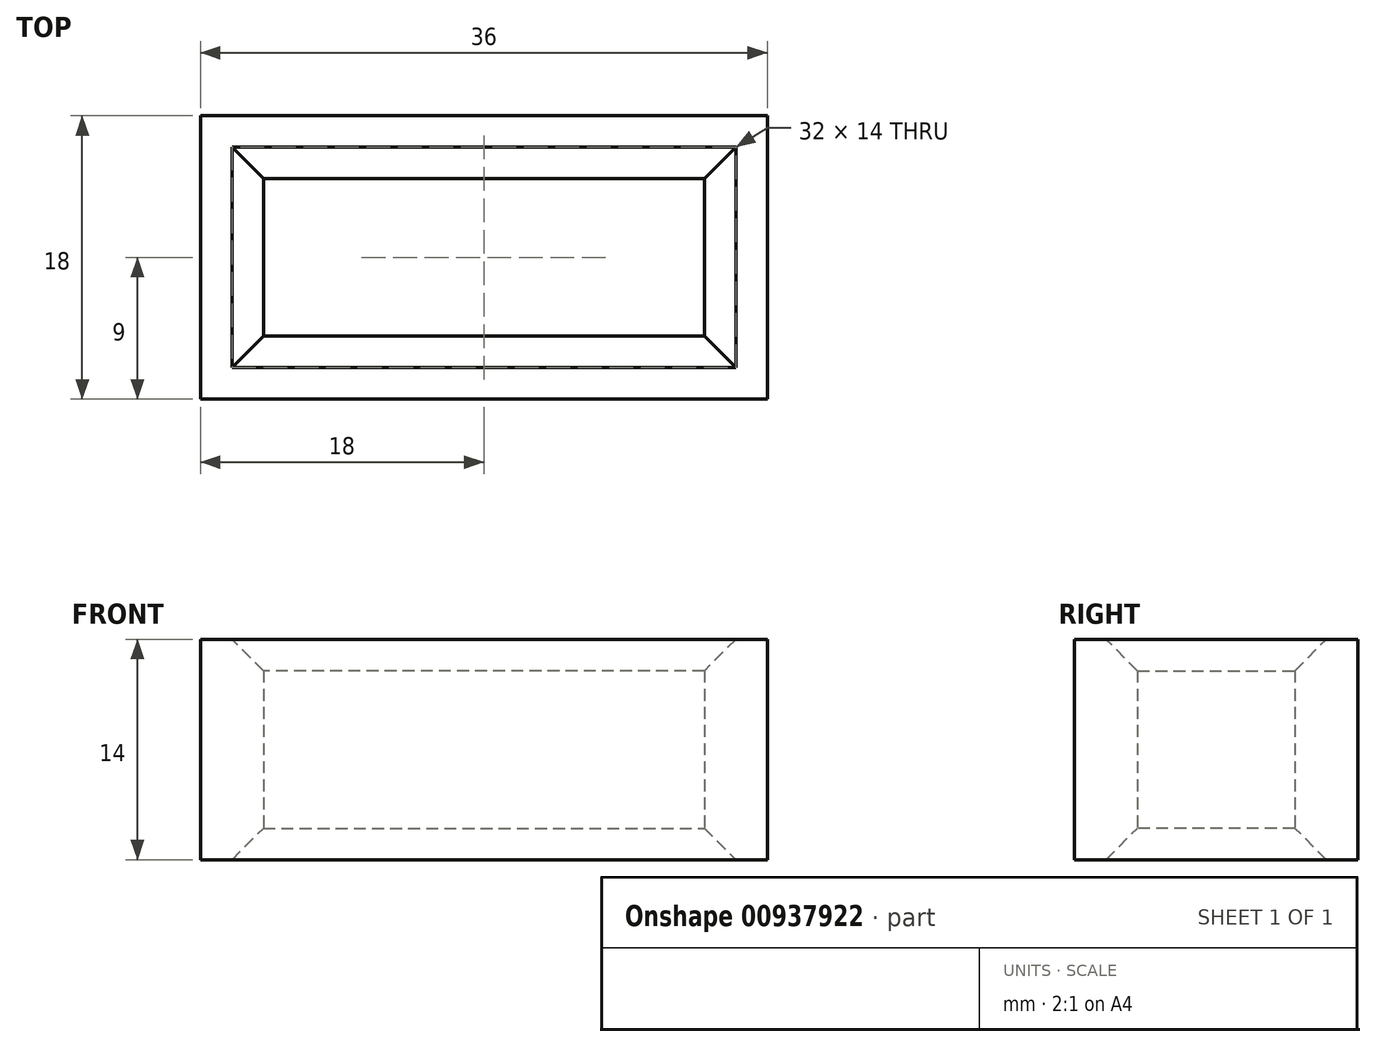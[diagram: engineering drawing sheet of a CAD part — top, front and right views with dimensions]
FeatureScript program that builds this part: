
annotation { "Feature Type Name" : "Feature", "Feature Type Description" : "" }
export const myFeature = defineFeature(function(context is Context, id is Id, definition is map)
    precondition{}
    {
        {
            var Q0;
            Q0=qCreatedBy(makeId("Top.planeOp"),FACE);
            var sketch = newSketch(context, id + "F0", { "sketchPlane" : qUnion([Q0])});
            skLineSegment(sketch, "E0.bottom", {"start": v(12.5, 3.7) * mm, "end": v(-12.5, 3.7) * mm});
            skLineSegment(sketch, "E0.top", {"start": v(12.5, -3.7) * mm, "end": v(-12.5, -3.7) * mm});
            skLineSegment(sketch, "E0.left", {"start": v(12.5, 3.7) * mm, "end": v(12.5, -3.7) * mm});
            skLineSegment(sketch, "E0.right", {"start": v(-12.5, 3.7) * mm, "end": v(-12.5, -3.7) * mm});
            skPoint(sketch, "E0.middle", {"position": v(0, 0) * mm});
            skLineSegment(sketch, "E1.bottom", {"start": v(14, 5) * mm, "end": v(-14, 5) * mm});
            skLineSegment(sketch, "E1.top", {"start": v(14, -5) * mm, "end": v(-14, -5) * mm});
            skLineSegment(sketch, "E1.left", {"start": v(14, 5) * mm, "end": v(14, -5) * mm});
            skLineSegment(sketch, "E1.right", {"start": v(-14, 5) * mm, "end": v(-14, -5) * mm});
            skLineSegment(sketch, "E2.bottom", {"start": v(18, 9) * mm, "end": v(-18, 9) * mm});
            skLineSegment(sketch, "E2.top", {"start": v(18, -9) * mm, "end": v(-18, -9) * mm});
            skLineSegment(sketch, "E2.left", {"start": v(18, 9) * mm, "end": v(18, -9) * mm});
            skLineSegment(sketch, "E2.right", {"start": v(-18, 9) * mm, "end": v(-18, -9) * mm});
            skSolve(sketch);
        }
        {
            var Q0;
            Q0=makeQuery(id+"F0.imprint","IMPRINT",FACE,{"disambiguationData":[TD([[makeQuery(id+"F0.imprint","IMPRINT",EDGE,{"derivedFrom":sQuery(id+"F0.wireOp",EDGE,"E1.bottom")}),-1.0]])]});
            extrude(context, id + "F1", {"entities" : qUnion([Q0]), "depth" : 14 * mm, "offsetDistance" : 25 * mm});
        }
        {
            var Q0;
            Q0=makeQuery(id+"F1.opExtrude","CAP_EDGE",EDGE,{"disambiguationData":[OSD([sQuery(id+"F0.wireOp",EDGE,"E1.bottom")])],"isStart":false});
            var Q1;
            Q1=makeQuery(id+"F1.opExtrude","CAP_EDGE",EDGE,{"disambiguationData":[OSD([sQuery(id+"F0.wireOp",EDGE,"E1.bottom")])],"isStart":true});
            var Q2;
            Q2=makeQuery(id+"F1.opExtrude","CAP_EDGE",EDGE,{"disambiguationData":[OSD([sQuery(id+"F0.wireOp",EDGE,"E1.top")])],"isStart":true});
            var Q3;
            Q3=makeQuery(id+"F1.opExtrude","CAP_EDGE",EDGE,{"disambiguationData":[OSD([sQuery(id+"F0.wireOp",EDGE,"E1.left")])],"isStart":false});
            var Q4;
            Q4=makeQuery(id+"F1.opExtrude","CAP_EDGE",EDGE,{"disambiguationData":[OSD([sQuery(id+"F0.wireOp",EDGE,"E1.top")])],"isStart":false});
            var Q5;
            Q5=makeQuery(id+"F1.opExtrude","CAP_EDGE",EDGE,{"disambiguationData":[OSD([sQuery(id+"F0.wireOp",EDGE,"E1.right")])],"isStart":true});
            var Q6;
            Q6=makeQuery(id+"F1.opExtrude","CAP_EDGE",EDGE,{"disambiguationData":[OSD([sQuery(id+"F0.wireOp",EDGE,"E1.left")])],"isStart":true});
            var Q7;
            Q7=makeQuery(id+"F1.opExtrude","CAP_EDGE",EDGE,{"disambiguationData":[OSD([sQuery(id+"F0.wireOp",EDGE,"E1.right")])],"isStart":false});
            chamfer(context, id + "F2", {"entities" : qUnion([Q0, Q1, Q2, Q3, Q4, Q5, Q6, Q7]), "width" : 2 * mm, "tangentPropagation" : true});
        }
    });
